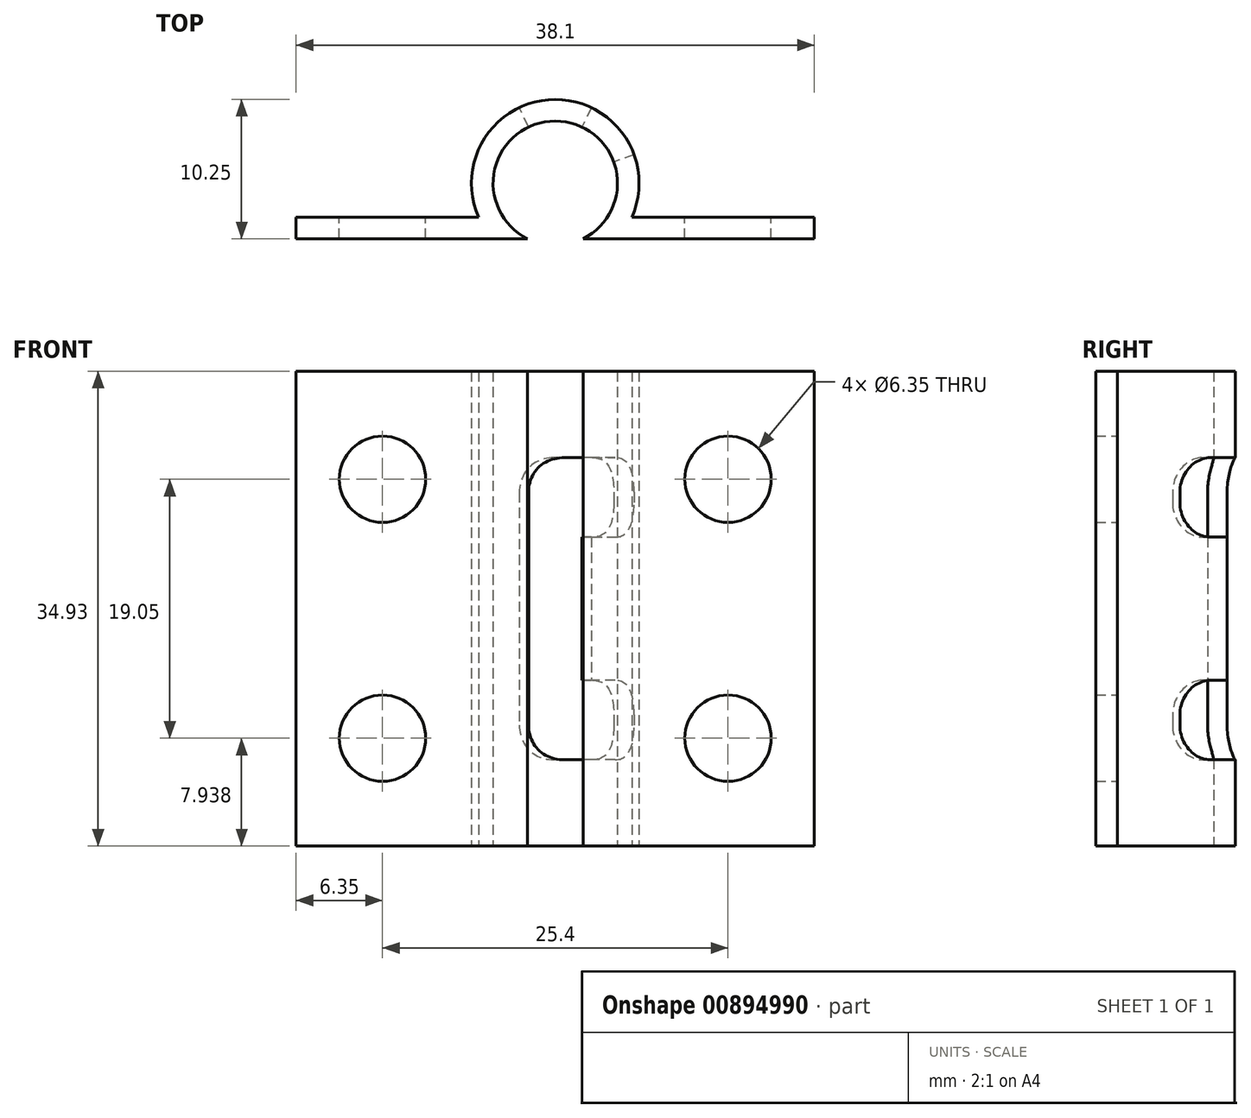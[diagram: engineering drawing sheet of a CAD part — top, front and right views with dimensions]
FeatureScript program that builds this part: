
annotation { "Feature Type Name" : "Feature", "Feature Type Description" : "" }
export const myFeature = defineFeature(function(context is Context, id is Id, definition is map)
    precondition{}
    {
        {
            var Q0;
            Q0=qCreatedBy(makeId("Top.planeOp"),FACE);
            var sketch = newSketch(context, id + "F0", { "sketchPlane" : qUnion([Q0])});
            skLineSegment(sketch, "E0.bottom", {"start": v(-19.05, 0.8) * mm, "end": v(-5.63, 0.8) * mm});
            skLineSegment(sketch, "E0.top", {"start": v(-19.05, -0.8) * mm, "end": v(-2.04, -0.8) * mm});
            skLineSegment(sketch, "E0.left", {"start": v(-19.05, 0.8) * mm, "end": v(-19.05, -0.8) * mm});
            skLineSegment(sketch, "E0.right", {"start": v(19.05, 0.8) * mm, "end": v(19.05, -0.8) * mm});
            skPoint(sketch, "E0.middle", {"position": v(0, 0) * mm});
            skArc(sketch, "E1", {"start": v(5.63, 0.8) * mm, "mid": v(0, 9.46) * mm, "end": v(-5.63, 0.8) * mm});
            skArc(sketch, "E2", {"start": v(2.04, -0.8) * mm, "mid": v(0, 7.87) * mm, "end": v(-2.04, -0.8) * mm});
            skLineSegment(sketch, "E3.trimOffspring", {"start": v(2.04, -0.8) * mm, "end": v(19.05, -0.8) * mm});
            skLineSegment(sketch, "E4.trimOffspring", {"start": v(5.63, 0.8) * mm, "end": v(19.05, 0.8) * mm});
            skSolve(sketch);
        }
        {
            var Q0;
            Q0 = qSketchRegion(id + "F0", true);
            extrude(context, id + "F1", {"entities" : qUnion([Q0]), "depth" : 34.92 * mm, "offsetDistance" : 25.4 * mm});
        }
        {
            var Q0;
            Q0=makeQuery(id+"F1.opExtrude","SWEPT_FACE",FACE,{"disambiguationData":[OSD([sQuery(id+"F0.wireOp",EDGE,"E0.bottom")])]});
            var sketch = newSketch(context, id + "F2", { "sketchPlane" : qUnion([Q0])});
            skPoint(sketch, "E5", {"position": v(12.7, 7.94) * mm});
            skPoint(sketch, "E6", {"position": v(12.7, 26.99) * mm});
            skPoint(sketch, "E7", {"position": v(-12.7, 26.99) * mm});
            skPoint(sketch, "E8", {"position": v(-12.7, 7.94) * mm});
            skSolve(sketch);
        }
        {
            var Q0;
            Q0=sQuery(id+"F2.wireOp",VERTEX,"E5");
            var Q1;
            Q1=sQuery(id+"F2.wireOp",VERTEX,"E6");
            var Q2;
            Q2=sQuery(id+"F2.wireOp",VERTEX,"E7");
            var Q3;
            Q3=sQuery(id+"F2.wireOp",VERTEX,"E8");
            var Q4;
            Q4=makeQuery(id+"F1.opExtrude","SWEPT_BODY",BODY,{"disambiguationData":[OSD([sQuery(id+"F0.wireOp",EDGE,"E0.bottom"),sQuery(id+"F0.wireOp",EDGE,"E0.top"),sQuery(id+"F0.wireOp",EDGE,"E0.left"),sQuery(id+"F0.wireOp",EDGE,"E0.right"),sQuery(id+"F0.wireOp",EDGE,"E1"),sQuery(id+"F0.wireOp",EDGE,"E2"),sQuery(id+"F0.wireOp",EDGE,"E3.trimOffspring"),sQuery(id+"F0.wireOp",EDGE,"E4.trimOffspring")])]});
            hole(context, id + "F3", {"style" : HoleStyle.SIMPLE, "endStyle" : HoleEndStyle.THROUGH, "holeDiameter" : 6.35 * mm, "majorDiameter" : 6.35 * mm, "isTappedThrough" : true, "tappedDepth" : 12.7 * mm, "tapClearance" : 3, "locations" : qUnion([Q0, Q1, Q2, Q3]), "scope" : qUnion([Q4])});
        }
        {
            var Q0;
            Q0=qCreatedBy(makeId("Top.planeOp"),FACE);
            cPlane(context, id + "F4", {"entities" : qUnion([Q0]), "cplaneType" : CPlaneType.OFFSET, "offset" : 6.35 * mm, "width" : 152.4 * mm, "height" : 152.4 * mm});
        }
        {
            var Q0;
            Q0=qCreatedBy(id+"F4.planeOp",FACE);
            var sketch = newSketch(context, id + "F5", { "sketchPlane" : qUnion([Q0])});
            skPoint(sketch, "E9", {"position": v(0, 3.3) * mm});
            skLineSegment(sketch, "E10", {"start": v(0, 3.3) * mm, "end": v(-4.32, 12.39) * mm});
            skLineSegment(sketch, "E11", {"start": v(0, 3.3) * mm, "end": v(4.32, 12.39) * mm});
            skLineSegment(sketch, "E12", {"start": v(-4.32, 12.39) * mm, "end": v(4.32, 12.39) * mm});
            skSolve(sketch);
        }
        {
            var Q0;
            Q0 = qSketchRegion(id + "F5", true);
            extrude(context, id + "F6", {"entities" : qUnion([Q0]), "operationType" : NewBodyOperationType.REMOVE, "depth" : 22.22 * mm, "offsetDistance" : 25.4 * mm});
        }
        {
            var Q0;
            Q0=qCreatedBy(id+"F4.planeOp",FACE);
            var sketch = newSketch(context, id + "F7", { "sketchPlane" : qUnion([Q0])});
            skPoint(sketch, "E13", {"position": v(0, 3.3) * mm});
            skLineSegment(sketch, "E14", {"start": v(0, 3.3) * mm, "end": v(0, 15.28) * mm});
            skLineSegment(sketch, "E15", {"start": v(0, 15.28) * mm, "end": v(13.48, 8.17) * mm});
            skLineSegment(sketch, "E16", {"start": v(13.48, 8.17) * mm, "end": v(0, 3.3) * mm});
            skSolve(sketch);
        }
        {
            var Q0;
            Q0 = qSketchRegion(id + "F7", true);
            extrude(context, id + "F8", {"entities" : qUnion([Q0]), "operationType" : NewBodyOperationType.REMOVE, "depth" : 5.84 * mm, "offsetDistance" : 25.4 * mm});
        }
        {
            var Q0;
            Q0=makeQuery(id+"F6.boolean.opBoolean","COPY",FACE,{"derivedFrom":makeQuery(id+"F6.opExtrude","CAP_FACE",FACE,{"disambiguationData":[OSD([sQuery(id+"F5.wireOp",EDGE,"E10"),sQuery(id+"F5.wireOp",EDGE,"E11"),sQuery(id+"F5.wireOp",EDGE,"E12")])],"isStart":false})});
            var sketch = newSketch(context, id + "F9", { "sketchPlane" : qUnion([Q0])});
            skPoint(sketch, "E17", {"position": v(0, -3.3) * mm});
            skLineSegment(sketch, "E18", {"start": v(0, -3.3) * mm, "end": v(8.58, -6.4) * mm});
            skLineSegment(sketch, "E19", {"start": v(8.58, -6.4) * mm, "end": v(0, -13.62) * mm});
            skPoint(sketch, "E19.endSnap0", {"position": v(0, -9.46) * mm});
            skLineSegment(sketch, "E20", {"start": v(0, -13.62) * mm, "end": v(0, -3.3) * mm});
            skSolve(sketch);
        }
        {
            var Q0;
            Q0 = qSketchRegion(id + "F9", true);
            extrude(context, id + "F10", {"entities" : qUnion([Q0]), "operationType" : NewBodyOperationType.REMOVE, "depth" : 5.84 * mm, "offsetDistance" : 25.4 * mm});
        }
        {
            var Q0;
            Q0=makeQuery(id+"F6.boolean.opBoolean","COPY",EDGE,{"derivedFrom":makeQuery(id+"F6.opExtrude","CAP_EDGE",EDGE,{"disambiguationData":[OSD([sQuery(id+"F5.wireOp",EDGE,"E10")])],"isStart":false})});
            var Q1;
            Q1=makeQuery(id+"F6.boolean.opBoolean","COPY",EDGE,{"derivedFrom":makeQuery(id+"F6.opExtrude","CAP_EDGE",EDGE,{"disambiguationData":[OSD([sQuery(id+"F5.wireOp",EDGE,"E10")])],"isStart":true})});
            var Q2;
            Q2=makeQuery(id+"F8.boolean.opBoolean","COPY",EDGE,{"derivedFrom":makeQuery(id+"F8.opExtrude","CAP_EDGE",EDGE,{"disambiguationData":[OSD([sQuery(id+"F7.wireOp",EDGE,"E16")])],"isStart":true})});
            var Q3;
            Q3=makeQuery(id+"F8.boolean.opBoolean","COPY",EDGE,{"derivedFrom":makeQuery(id+"F8.opExtrude","CAP_EDGE",EDGE,{"disambiguationData":[OSD([sQuery(id+"F7.wireOp",EDGE,"E16")])],"isStart":false})});
            var Q4;
            Q4=makeQuery(id+"F10.boolean.opBoolean","COPY",EDGE,{"derivedFrom":makeQuery(id+"F10.opExtrude","CAP_EDGE",EDGE,{"disambiguationData":[OSD([sQuery(id+"F9.wireOp",EDGE,"E18")])],"isStart":false})});
            var Q5;
            Q5=makeQuery(id+"F10.boolean.opBoolean","COPY",EDGE,{"derivedFrom":makeQuery(id+"F10.opExtrude","CAP_EDGE",EDGE,{"disambiguationData":[OSD([sQuery(id+"F9.wireOp",EDGE,"E18")])],"isStart":true})});
            fillet(context, id + "F11", {"entities" : qUnion([Q0, Q1, Q2, Q3, Q4, Q5]), "radius" : 2.54 * mm, "tangentPropagation" : true, "allowEdgeOverflow" : false});
        }
    });
